# Revit family: Domotics-SerieCivili-GEWISS-27COMBIDIN_SYSTEM-IP40_2M_4SY
name_source: partatom
category: Apparecchi elettrici
revit_build: Autodesk Revit 2016 (Build: 20161004_0715(x64)
units: mm (PartAtom-declared; Revit-internal decimal feet)

## family parameters
Condiviso = No
Host = Superficie
Mantenere orientamento annotazione = No
Punto di calcolo locali = No
Quota connettore circolare = Usa diametro
Taglio con vuoti quando caricato = No
Tipo di parte = Normale

## types (1)
- Domotics-SerieCivili-GEWISS-27COMBIDIN_SYSTEM-IP40_2M_4SY
    Altezza = 132 mm  [stored 0.433071 ft]
    Caratteristiche = Halogen free
    Catalogo = DOMOTICS
    Catalogo Serie = 27COMBI
    Classe isolamento = II
    Codice EAN = 8011564055445
    Codice Electrocod = 0212
    Colore = Grigio RAL 7035
    Colore portella = Trasparente fume'
    Configurazione = Modulo 2 x 2
    Contatti di uscita = 1NA 16 A (AC1) 250 V ac
    Coppia serraggio viti = 0,8NM
    Corrente nominale (In) = 32A
    Descrizione = CONTENITORE 2MOD.DIN+(2X2)MOD.SYSTEM PR.
    Dim. esterne BxHxP (mm) = 132x132x95
    Glow Wire Test = 650°C
    Grado di protezione = IP40
    IDF = 45a36d84-0d20-4ff0-9bfc-049fc30f44fc
    IDT = 1e104662-b0c2-4183-8d58-26241cd5dc0a
    Immagine tipo = GW27071.jpg
    Larghezza = 132 mm  [stored 0.433071 ft]
    Modello = GW27071
    N. fori Ã˜ 23 sfondabili = 10
    N. fori Ã˜ 23 sfondabili: = Laterali 10 / Sul fondo 2
    N. moduli DIN = 2
    N. moduli SYSTEM = 4
    Norma di riferimento = EN 60669-2-1
    Norma di riferimento: = EN 60670-1 - EN 60670-24
    Potenza dissipabile (W) = 13
    Predisposizione scomparti = 1
    Produttore = GEWISS S.p.A.
    Profondità = 95 mm
    Prospetto di default = 1219 mm
    Resistenza agli urti = IK07
    SEO = Contenitore
    Scheda Tecnica = https://www.gewiss.com
    Temperatura di installazione = -25 +60 °C
    Tensione di isolamento = 750V
    Tensione nominale: = 400 V ac
    Termopressione con biglia = 70 °C
    Tipo portella = Rigida
    Tipo sfondabili = Asportabili con utensile
    Tipologia di contenitore = GP
    URL = https://www.gewiss.com
    Versione file RFA = 19.4
    Viti coperchio = Acciaio inox

note: [stored X ft] marks values corroborated as IEEE doubles in the binary element streams (Revit-internal decimal feet)
